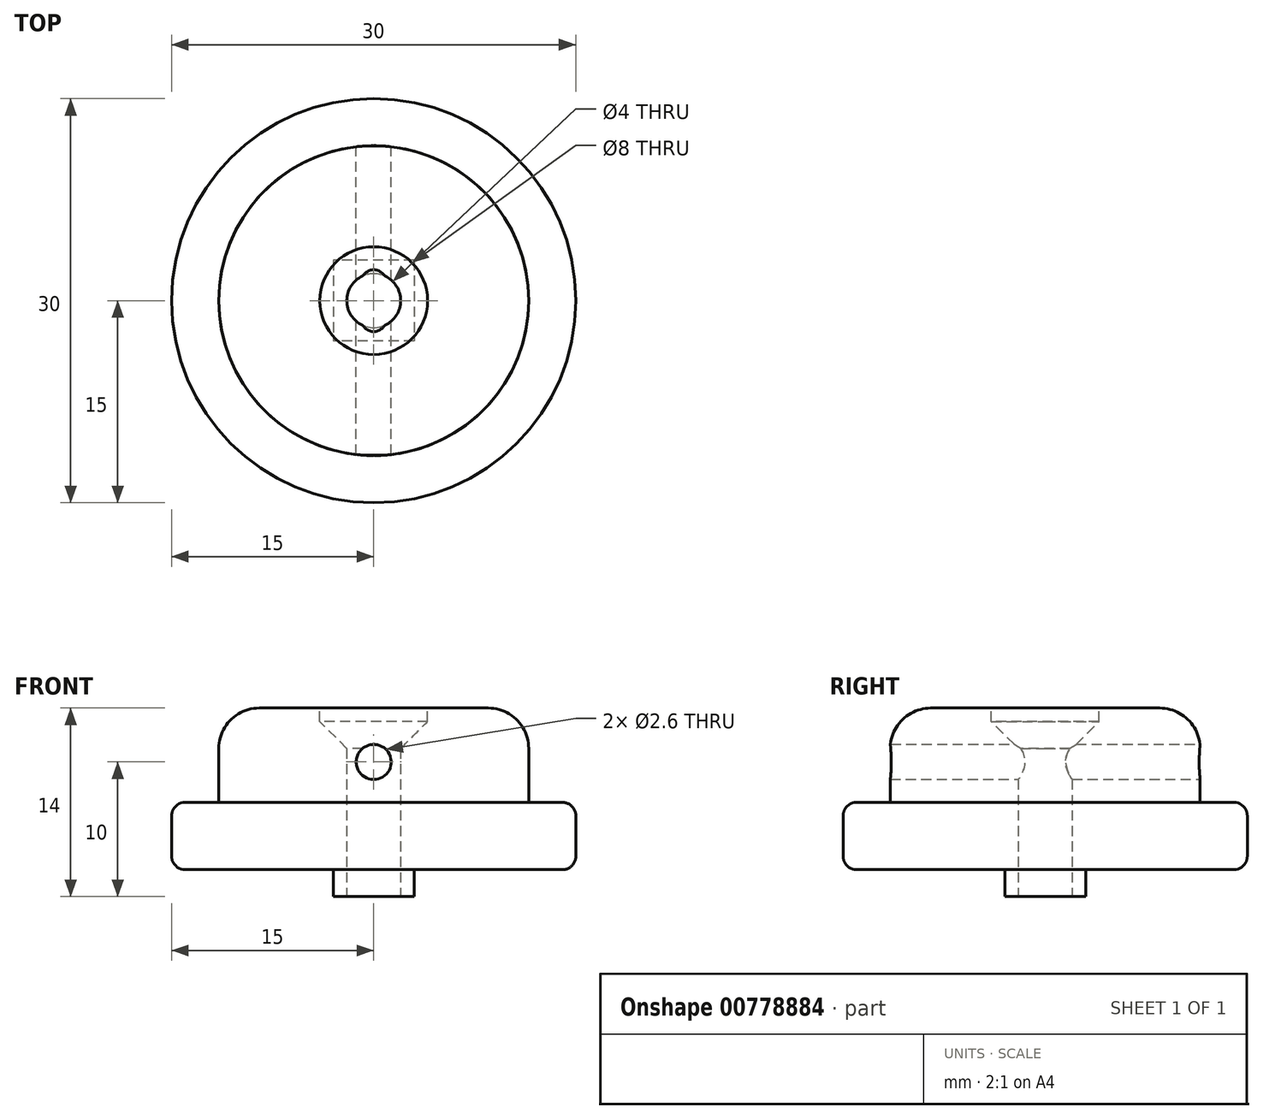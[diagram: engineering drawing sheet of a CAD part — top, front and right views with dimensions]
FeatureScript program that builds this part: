
annotation { "Feature Type Name" : "Feature", "Feature Type Description" : "" }
export const myFeature = defineFeature(function(context is Context, id is Id, definition is map)
    precondition{}
    {
        {
            var Q0;
            Q0=qCreatedBy(makeId("Top.planeOp"),FACE);
            var sketch = newSketch(context, id + "F0", { "sketchPlane" : qUnion([Q0])});
            skCircle(sketch, "E0", {"center": v(0, 0) * mm, "radius": 15 * mm});
            skCircle(sketch, "E1", {"center": v(0, 0) * mm, "radius": 11.5 * mm});
            skCircle(sketch, "E2", {"center": v(0, 0) * mm, "radius": 2 * mm});
            skSolve(sketch);
        }
        {
            var Q0;
            Q0=makeQuery(id+"F0.imprint","IMPRINT",FACE,{"disambiguationData":[TD([[makeQuery(id+"F0.imprint","IMPRINT",EDGE,{"derivedFrom":sQuery(id+"F0.wireOp",EDGE,"E0")}),1.0]])]});
            extrude(context, id + "F1", {"entities" : qUnion([Q0]), "depth" : 5 * mm, "offsetDistance" : 25 * mm});
        }
        {
            var Q0;
            Q0=makeQuery(id+"F0.imprint","IMPRINT",FACE,{"disambiguationData":[TD([[makeQuery(id+"F0.imprint","IMPRINT",EDGE,{"derivedFrom":sQuery(id+"F0.wireOp",EDGE,"E1")}),1.0]])]});
            extrude(context, id + "F2", {"entities" : qUnion([Q0]), "operationType" : NewBodyOperationType.ADD, "depth" : 12 * mm, "offsetDistance" : 25 * mm});
        }
        {
            var Q0;
            Q0=makeQuery(id+"F2.opExtrude","CAP_EDGE",EDGE,{"disambiguationData":[OSD([sQuery(id+"F0.wireOp",EDGE,"E1")])],"isStart":false});
            fillet(context, id + "F3", {"entities" : qUnion([Q0]), "radius" : 3 * mm, "tangentPropagation" : true, "allowEdgeOverflow" : false});
        }
        {
            var Q0;
            Q0=makeQuery(id+"F1.opExtrude","CAP_EDGE",EDGE,{"disambiguationData":[OSD([sQuery(id+"F0.wireOp",EDGE,"E0")])],"isStart":true});
            var Q1;
            Q1=makeQuery(id+"F1.opExtrude","CAP_EDGE",EDGE,{"disambiguationData":[OSD([sQuery(id+"F0.wireOp",EDGE,"E0")])],"isStart":false});
            fillet(context, id + "F4", {"entities" : qUnion([Q0, Q1]), "radius" : 1 * mm, "tangentPropagation" : true, "allowEdgeOverflow" : false});
        }
        {
            var Q0;
            Q0=makeQuery(id+"F2.opExtrude","CAP_FACE",FACE,{"disambiguationData":[OSD([sQuery(id+"F0.wireOp",EDGE,"E1"),sQuery(id+"F0.wireOp",EDGE,"E2")])],"isStart":false});
            var sketch = newSketch(context, id + "F5", { "sketchPlane" : qUnion([Q0])});
            skCircle(sketch, "E3", {"center": v(0, 0) * mm, "radius": 4 * mm});
            skSolve(sketch);
        }
        {
            var Q0;
            Q0 = qSketchRegion(id + "F5", true);
            extrude(context, id + "F6", {"entities" : qUnion([Q0]), "operationType" : NewBodyOperationType.REMOVE, "oppositeDirection" : true, "depth" : 1 * mm, "offsetDistance" : 25 * mm});
        }
        {
            var Q0;
            Q0=makeQuery(id+"F6.boolean.opBoolean","INTERSECT",EDGE,{"derivedFrom":[makeQuery(id+"F2.opExtrude","SWEPT_FACE",FACE,{"disambiguationData":[OSD([sQuery(id+"F0.wireOp",EDGE,"E2")])]}),makeQuery(id+"F6.opExtrude","CAP_FACE",FACE,{"disambiguationData":[OSD([sQuery(id+"F5.wireOp",EDGE,"E3")])],"isStart":false})]});
            chamfer(context, id + "F7", {"entities" : qUnion([Q0]), "width" : 2 * mm, "tangentPropagation" : true});
        }
        {
            var Q0;
            Q0=qCreatedBy(makeId("Front.planeOp"),FACE);
            var sketch = newSketch(context, id + "F8", { "sketchPlane" : qUnion([Q0])});
            skLineSegment(sketch, "E4", {"start": v(0, 0) * mm, "end": v(0, 8) * mm, "construction": true});
            skCircle(sketch, "E5", {"center": v(0, 8) * mm, "radius": 1.3 * mm});
            skSolve(sketch);
        }
        {
            var Q0;
            Q0 = qSketchRegion(id + "F8", true);
            extrude(context, id + "F9", {"entities" : qUnion([Q0]), "operationType" : NewBodyOperationType.REMOVE, "depth" : 25 * mm, "offsetDistance" : 25 * mm, "hasSecondDirection" : true, "secondDirectionOppositeDirection" : true, "secondDirectionDepth" : 25 * mm});
        }
        {
            var Q0;
            Q0=qCreatedBy(makeId("Top.planeOp"),FACE);
            var sketch = newSketch(context, id + "F10", { "sketchPlane" : qUnion([Q0])});
            skLineSegment(sketch, "E6.bottom", {"start": v(-3, -3) * mm, "end": v(3, -3) * mm});
            skLineSegment(sketch, "E6.top", {"start": v(-3, 3) * mm, "end": v(3, 3) * mm});
            skLineSegment(sketch, "E6.left", {"start": v(-3, -3) * mm, "end": v(-3, 3) * mm});
            skLineSegment(sketch, "E6.right", {"start": v(3, -3) * mm, "end": v(3, 3) * mm});
            skPoint(sketch, "E6.middle", {"position": v(0, 0) * mm});
            skSolve(sketch);
        }
        {
            var Q0;
            Q0 = qSketchRegion(id + "F10", true);
            extrude(context, id + "F11", {"entities" : qUnion([Q0]), "operationType" : NewBodyOperationType.ADD, "depth" : 5 * mm, "offsetDistance" : 25 * mm, "hasSecondDirection" : true, "secondDirectionOppositeDirection" : true, "secondDirectionDepth" : 2 * mm});
        }
        {
            var Q0;
            Q0=qCreatedBy(makeId("Top.planeOp"),FACE);
            var sketch = newSketch(context, id + "F12", { "sketchPlane" : qUnion([Q0])});
            skCircle(sketch, "E7", {"center": v(0, 0) * mm, "radius": 2 * mm});
            skSolve(sketch);
        }
        {
            var Q0;
            Q0 = qSketchRegion(id + "F12", true);
            extrude(context, id + "F13", {"entities" : qUnion([Q0]), "operationType" : NewBodyOperationType.REMOVE, "oppositeDirection" : true, "depth" : 25 * mm, "offsetDistance" : 25 * mm, "hasSecondDirection" : true, "secondDirectionOppositeDirection" : false, "secondDirectionDepth" : 25 * mm});
        }
    });
